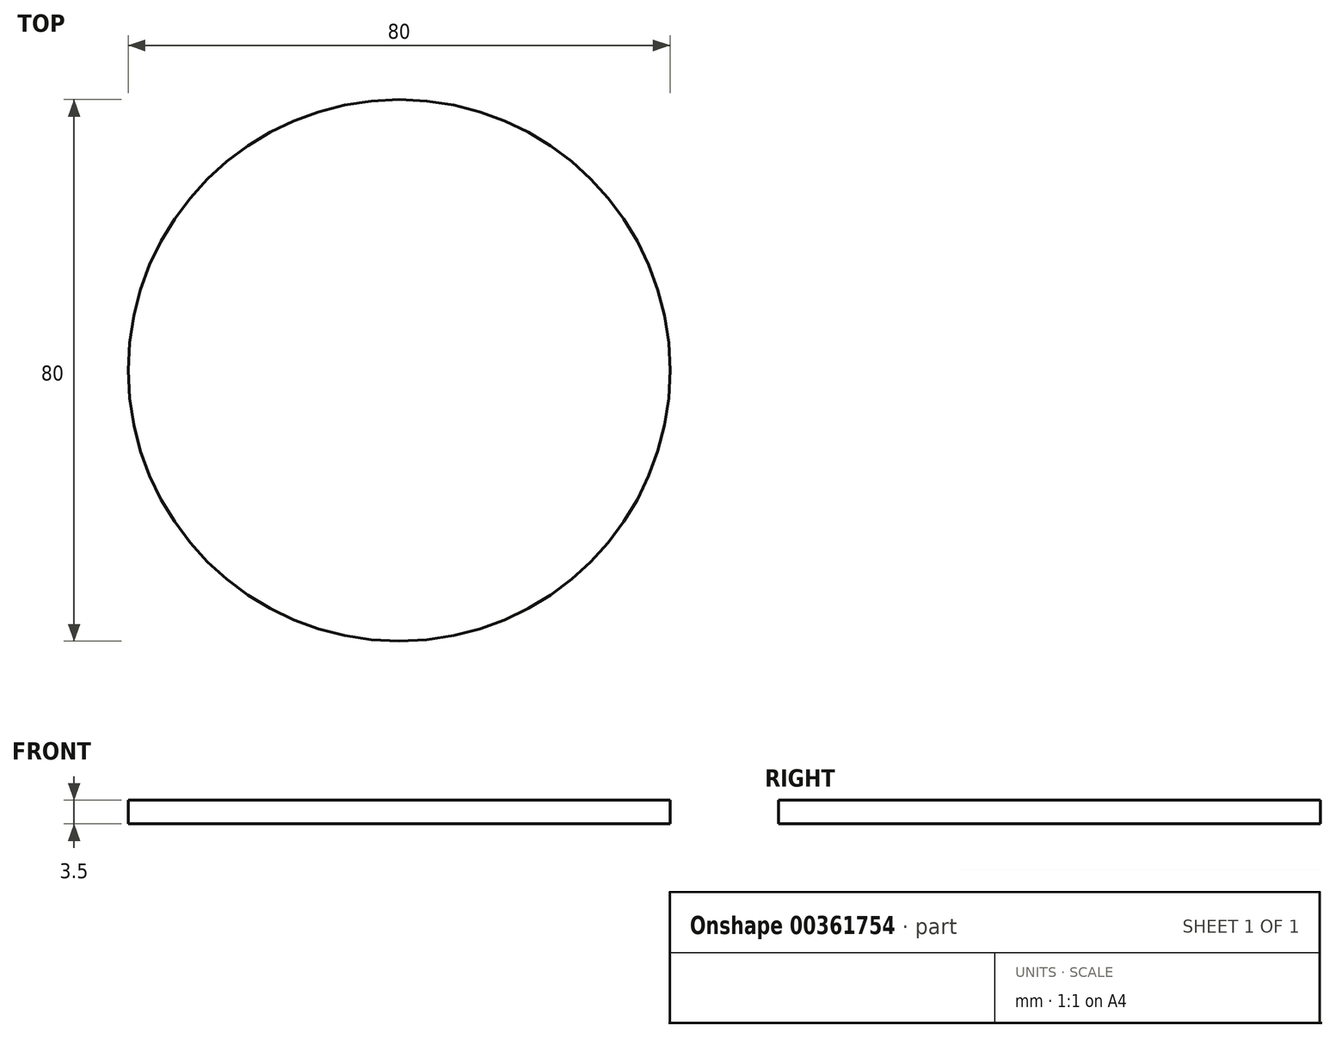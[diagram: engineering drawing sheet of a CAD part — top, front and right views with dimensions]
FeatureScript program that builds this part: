
annotation { "Feature Type Name" : "Feature", "Feature Type Description" : "" }
export const myFeature = defineFeature(function(context is Context, id is Id, definition is map)
    precondition{}
    {
        {
            var Q0;
            Q0=qCreatedBy(makeId("Top.planeOp"),FACE);
            var sketch = newSketch(context, id + "F0", { "sketchPlane" : qUnion([Q0])});
            skCircle(sketch, "E0", {"center": v(0, 0) * mm, "radius": 40 * mm});
            skSolve(sketch);
        }
        {
            var Q0;
            Q0=makeQuery(id+"F0.imprint","IMPRINT",FACE,{"disambiguationData":[TD([[makeQuery(id+"F0.imprint","IMPRINT",EDGE,{"derivedFrom":sQuery(id+"F0.wireOp",EDGE,"E0")}),1.0]])]});
            extrude(context, id + "F1", {"entities" : qUnion([Q0]), "depth" : 3.5 * mm, "offsetDistance" : 25 * mm});
        }
    });
